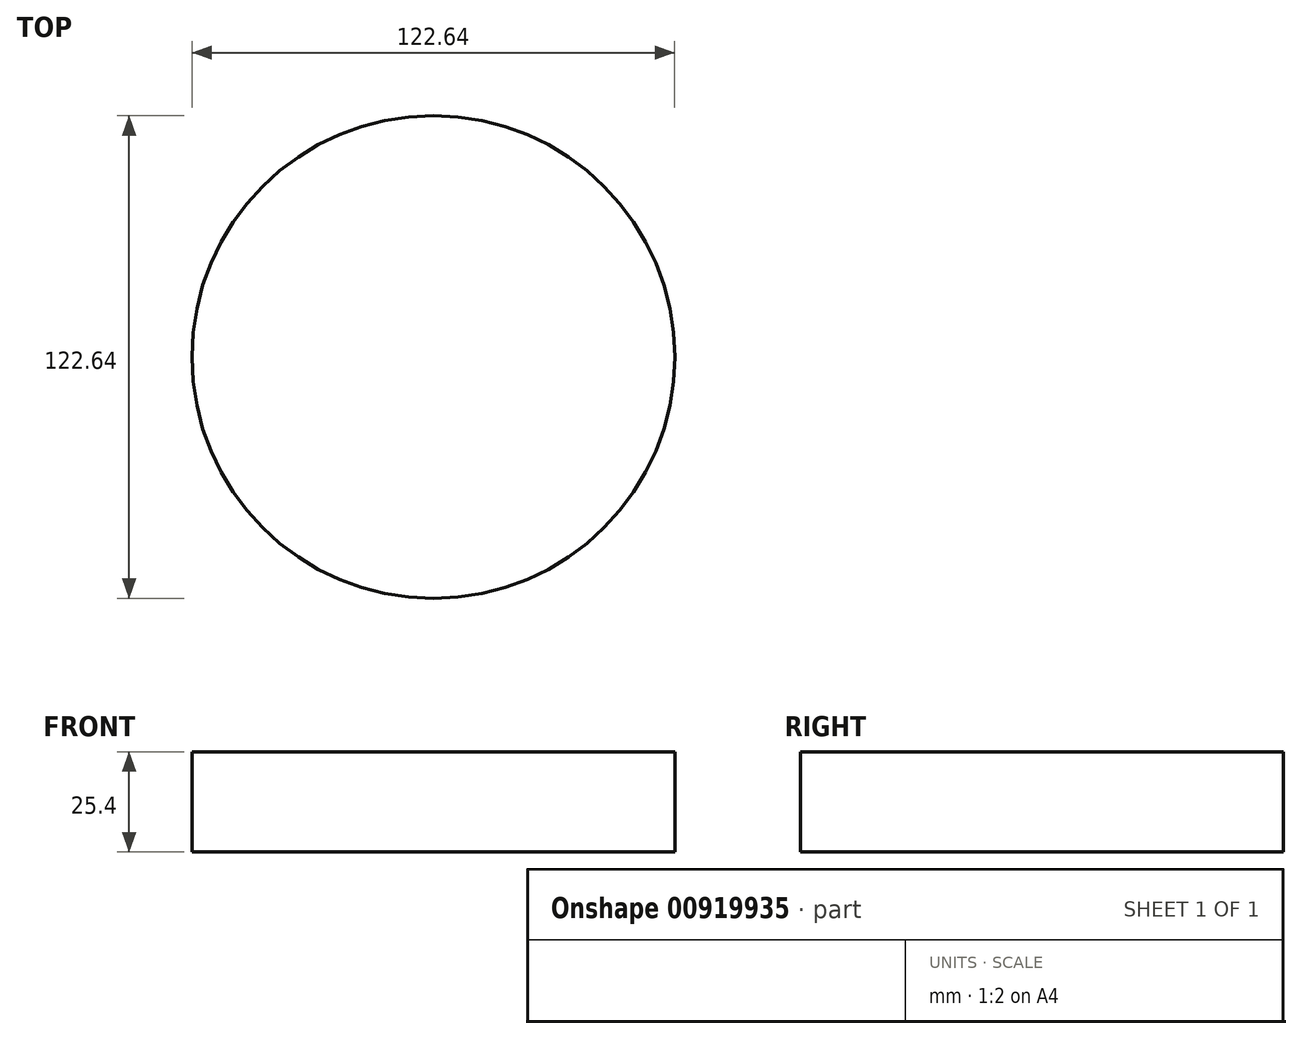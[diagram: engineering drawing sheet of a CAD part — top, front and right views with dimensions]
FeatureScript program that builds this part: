
annotation { "Feature Type Name" : "Feature", "Feature Type Description" : "" }
export const myFeature = defineFeature(function(context is Context, id is Id, definition is map)
    precondition{}
    {
        {
            var Q0;
            Q0=qCreatedBy(makeId("Top.planeOp"),FACE);
            var sketch = newSketch(context, id + "F0", { "sketchPlane" : qUnion([Q0])});
            skCircle(sketch, "E0", {"center": v(0, 0) * mm, "radius": 61.32 * mm});
            skSolve(sketch);
        }
        {
            var Q0;
            Q0=makeQuery(id+"F0.imprint","IMPRINT",FACE,{"disambiguationData":[TD([[makeQuery(id+"F0.imprint","IMPRINT",EDGE,{"derivedFrom":sQuery(id+"F0.wireOp",EDGE,"E0")}),1.0]])]});
            extrude(context, id + "F1", {"entities" : qUnion([Q0]), "depth" : 25.4 * mm, "offsetDistance" : 25.4 * mm});
        }
    });
